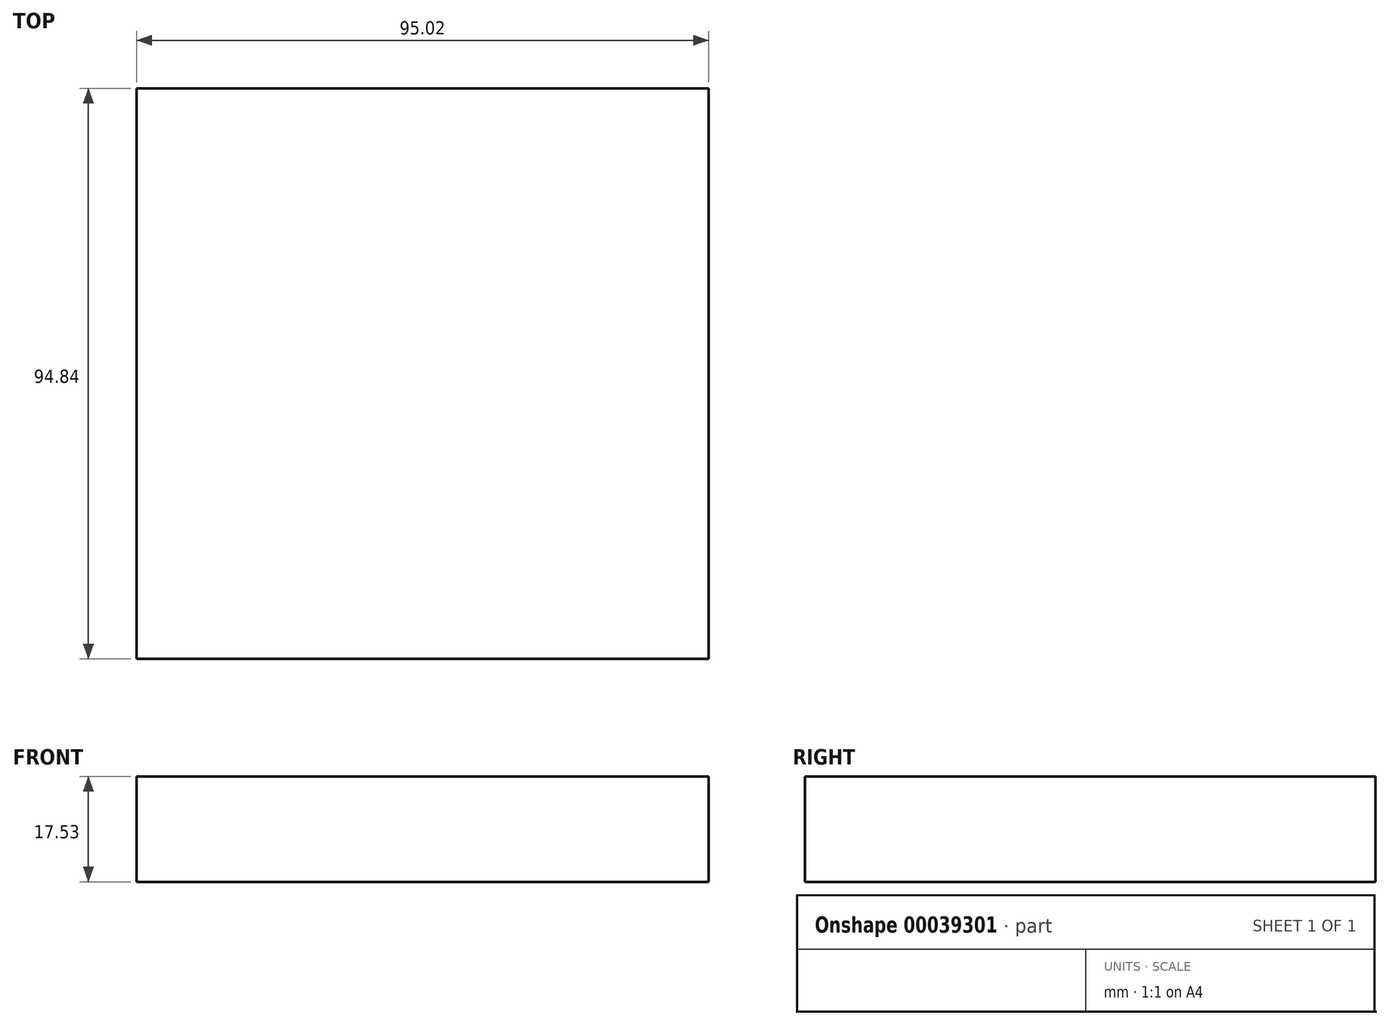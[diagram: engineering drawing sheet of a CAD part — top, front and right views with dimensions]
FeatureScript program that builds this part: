
annotation { "Feature Type Name" : "Feature", "Feature Type Description" : "" }
export const myFeature = defineFeature(function(context is Context, id is Id, definition is map)
    precondition{}
    {
        {
            var Q0;
            Q0=qCreatedBy(makeId("Top.planeOp"),FACE);
            var sketch = newSketch(context, id + "F0", { "sketchPlane" : qUnion([Q0])});
            skLineSegment(sketch, "E0", {"start": v(-47.51, 47.42) * mm, "end": v(47.51, 47.42) * mm});
            skLineSegment(sketch, "E1", {"start": v(47.51, 47.42) * mm, "end": v(47.51, -47.42) * mm});
            skLineSegment(sketch, "E2", {"start": v(47.51, -47.42) * mm, "end": v(-47.51, -47.42) * mm});
            skLineSegment(sketch, "E3", {"start": v(-47.51, -47.42) * mm, "end": v(-47.51, 47.42) * mm});
            skLineSegment(sketch, "E4", {"start": v(0, 0) * mm, "end": v(0, 47.42) * mm, "construction": true});
            skLineSegment(sketch, "E5", {"start": v(0, 0) * mm, "end": v(47.51, 0) * mm, "construction": true});
            skSolve(sketch);
        }
        {
            var Q0;
            Q0 = qSketchRegion(id + "F0", true);
            extrude(context, id + "F1", {"entities" : qUnion([Q0]), "depth" : 17.53 * mm});
        }
    });
